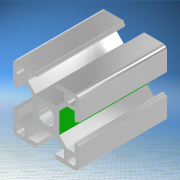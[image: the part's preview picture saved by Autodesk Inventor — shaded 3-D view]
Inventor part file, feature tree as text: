
AUTODESK INVENTOR PART (.ipt)
format: ipt  version: 2020.2 (Build 242310000, 310)  size: 247,808 bytes
history: native  units: mm
features: extrude x1, sketch x1
ambient origin geometry x8: Origin, YZ Plane, XZ Plane, XY Plane, X Axis, Y Axis, Z Axis, Center Point
bodies: Solid1 (feature_tree)
feature tree (2):
  extrude  "Extrusion1"  [1 undecoded]
  sketch  "Sketch1"  dims[d0=40.0mm d1=0.0mm]
note: 1 required parameter value undecoded (feature->parameter linkage not recoverable at this tier; creation-order binding heuristic only, values carry confidence <= 0.55)
